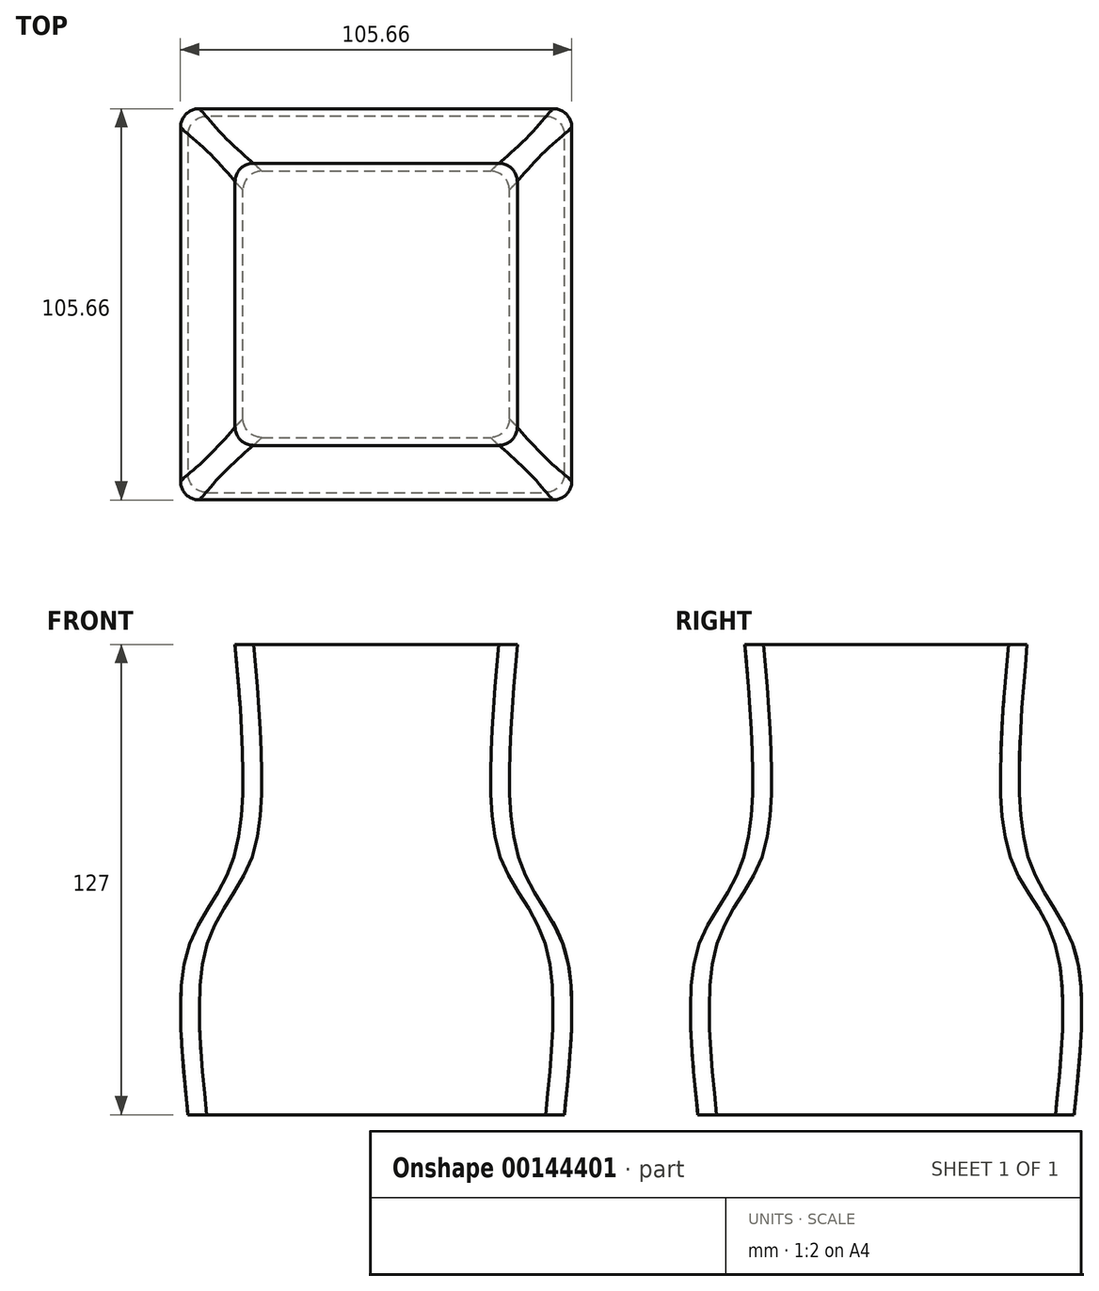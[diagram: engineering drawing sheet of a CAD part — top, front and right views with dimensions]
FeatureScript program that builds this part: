
annotation { "Feature Type Name" : "Feature", "Feature Type Description" : "" }
export const myFeature = defineFeature(function(context is Context, id is Id, definition is map)
    precondition{}
    {
        {
            var Q0;
            Q0=qCreatedBy(makeId("Top.planeOp"),FACE);
            var sketch = newSketch(context, id + "F0", { "sketchPlane" : qUnion([Q0])});
            skLineSegment(sketch, "E0.bottom", {"start": v(50.8, -50.8) * mm, "end": v(-50.8, -50.8) * mm});
            skLineSegment(sketch, "E0.top", {"start": v(50.8, 50.8) * mm, "end": v(-50.8, 50.8) * mm});
            skLineSegment(sketch, "E0.left", {"start": v(50.8, -50.8) * mm, "end": v(50.8, 50.8) * mm});
            skLineSegment(sketch, "E0.right", {"start": v(-50.8, -50.8) * mm, "end": v(-50.8, 50.8) * mm});
            skPoint(sketch, "E0.middle", {"position": v(0, 0) * mm});
            skPoint(sketch, "E1", {"position": v(50.8, 50.8) * mm});
            skPoint(sketch, "E2", {"position": v(-50.8, 50.8) * mm});
            skPoint(sketch, "E3", {"position": v(-50.8, -50.8) * mm});
            skPoint(sketch, "E4", {"position": v(50.8, -50.8) * mm});
            skSolve(sketch);
        }
        {
            var Q0;
            Q0=makeQuery(id+"F0.imprint","IMPRINT",FACE,{"disambiguationData":[TD([[makeQuery(id+"F0.imprint","IMPRINT",EDGE,{"derivedFrom":sQuery(id+"F0.wireOp",EDGE,"E0.bottom")}),-1.0]])]});
            cPlane(context, id + "F1", {"entities" : qUnion([Q0]), "cplaneType" : CPlaneType.OFFSET, "offset" : 127 * mm, "width" : 152.4 * mm, "height" : 152.4 * mm});
        }
        {
            var Q0;
            Q0=qCreatedBy(id+"F1.planeOp",FACE);
            var sketch = newSketch(context, id + "F2", { "sketchPlane" : qUnion([Q0])});
            skLineSegment(sketch, "E5.bottom", {"start": v(38.1, 38.1) * mm, "end": v(-38.1, 38.1) * mm});
            skLineSegment(sketch, "E5.top", {"start": v(38.1, -38.1) * mm, "end": v(-38.1, -38.1) * mm});
            skLineSegment(sketch, "E5.left", {"start": v(38.1, 38.1) * mm, "end": v(38.1, -38.1) * mm});
            skLineSegment(sketch, "E5.right", {"start": v(-38.1, 38.1) * mm, "end": v(-38.1, -38.1) * mm});
            skPoint(sketch, "E5.middle", {"position": v(0, 0) * mm});
            skPoint(sketch, "E6", {"position": v(-38.1, 38.1) * mm});
            skPoint(sketch, "E7", {"position": v(-38.1, -38.1) * mm});
            skPoint(sketch, "E8", {"position": v(38.1, -38.1) * mm});
            skPoint(sketch, "E9", {"position": v(38.1, 38.1) * mm});
            skSolve(sketch);
        }
        {
            var Q0;
            Q0=qCreatedBy(makeId("Front.planeOp"),FACE);
            var sketch = newSketch(context, id + "F3", { "sketchPlane" : qUnion([Q0])});
            skLineSegment(sketch, "E10", {"start": v(0, 0) * mm, "end": v(0, 141.89) * mm});
            skSolve(sketch);
        }
        {
            var Q0;
            Q0=qCreatedBy(makeId("Right.planeOp"),FACE);
            var Q1;
            Q1=sQuery(id+"F3.wireOp",EDGE,"E10");
            cPlane(context, id + "F4", {"entities" : qUnion([Q0, Q1]), "cplaneType" : CPlaneType.LINE_ANGLE, "offset" : 25.4 * mm, "angle" : 45 * degree, "width" : 152.4 * mm, "height" : 152.4 * mm});
        }
        {
            var Q0;
            Q0=qCreatedBy(id+"F4.planeOp",FACE);
            var sketch = newSketch(context, id + "F5", { "sketchPlane" : qUnion([Q0])});
            skLineSegment(sketch, "E11.0", {"start": v(0, 0) * mm, "end": v(-71.84, 0) * mm});
            skLineSegment(sketch, "E12.0", {"start": v(-53.88, 127) * mm, "end": v(0, 127) * mm});
            skLineSegment(sketch, "E13.0", {"start": v(0, 0) * mm, "end": v(0, 141.89) * mm});
            skFitSpline(sketch, "E14", {"points": [v(-71.84, 0) * mm, v(-71.84, 45.01) * mm, v(-54.58, 68.89) * mm, v(-53.88, 127) * mm], "startDerivative": vector(-21.9, 149.66) * mm, "endDerivative": vector(-21.2, 173.28) * mm});
            skSolve(sketch);
        }
        {
            var Q0;
            {var subQ0=sQuery(id+"F5.wireOp",EDGE,"E11.0");Q0=makeQuery(id+"F5.imprint","IMPRINT",FACE,{"disambiguationData":[TD([[makeQuery(id+"F5.imprint","IMPRINT",EDGE,{"derivedFrom":subQ0}),-1.0]])]});}
            var Q1;
            Q1=sQuery(id+"F0.wireOp",EDGE,"E0.right");
            var Q2;
            Q2=sQuery(id+"F0.wireOp",EDGE,"E0.bottom");
            var Q3;
            Q3=sQuery(id+"F0.wireOp",EDGE,"E0.left");
            var Q4;
            Q4=sQuery(id+"F0.wireOp",EDGE,"E0.top");
            sweep(context, id + "F6", {"profiles" : qUnion([Q0]), "path" : qUnion([Q1, Q2, Q3, Q4])});
        }
        {
            var Q0;
            Q0=makeQuery(id+"F6.opSweep","MID_CAP_EDGE",EDGE,{"disambiguationData":[OSD([sQuery(id+"F0.wireOp",VERTEX,"E0.bottom.end"),sQuery(id+"F5.wireOp",EDGE,"E14")])],"capPos":3.0});
            var Q1;
            Q1=makeQuery(id+"F6.opSweep","CAP_EDGE",EDGE,{"disambiguationData":[OSD([sQuery(id+"F0.wireOp",VERTEX,"E0.top.end"),sQuery(id+"F5.wireOp",EDGE,"E14")])],"isStart":true});
            var Q2;
            Q2=makeQuery(id+"F6.opSweep","MID_CAP_EDGE",EDGE,{"disambiguationData":[OSD([sQuery(id+"F0.wireOp",VERTEX,"E0.left.start"),sQuery(id+"F5.wireOp",EDGE,"E14")])],"capPos":2.0});
            var Q3;
            Q3=makeQuery(id+"F6.opSweep","MID_CAP_EDGE",EDGE,{"disambiguationData":[OSD([sQuery(id+"F0.wireOp",VERTEX,"E0.top.start"),sQuery(id+"F5.wireOp",EDGE,"E14")])],"capPos":1.0});
            fillet(context, id + "F7", {"entities" : qUnion([Q0, Q1, Q2, Q3]), "radius" : 5.08 * mm, "tangentPropagation" : true, "allowEdgeOverflow" : false});
        }
    });
